# Revit family: Regal kiinteä tukikaide
name_source: partatom
category: Specialty Equipment
revit_build: Autodesk Revit 2015 (Build: 20160512_0715(x64)
units: mm (PartAtom-declared; Revit-internal decimal feet)

## types (4) — shared parameters
Assembly Code = 1336
Frame Colour = RAL 9016 - White
Height = 204 mm
Keynote = 523
Manufacturer = Väinö Korpinen Oy
Model = Regal
Support Height = 800 mm  [stored 2.62467 ft]
Thickness = 30 mm  [stored 0.0984252 ft]
URL = http://www.korpinen.com
Width = 125 mm  [stored 0.410105 ft]

## per-type parameters (varying)
| type | 770 | 870 | Colour | Depth | Model ID |
| 20105G harmaa | No | Yes | Elastomer - Red | 870 mm  [stored 2.85433 ft] | 20203R |
| 20203G harmaa | No | Yes | Elastomer - Grey | 870 mm  [stored 2.85433 ft] | 20203G |
| 20105R punainen | Yes | No | Elastomer - Red | 770 mm  [stored 2.52625 ft] | 20150R |
| 20203R punainen | No | Yes | Elastomer - Red | 870 mm  [stored 2.85433 ft] | 20203R |

note: [stored X ft] marks values corroborated as IEEE doubles in the binary element streams (Revit-internal decimal feet)

## geometry (parser evidence)
native form markers: Blend x6, Sweep x14
no freeform markers — native parametric forms only
